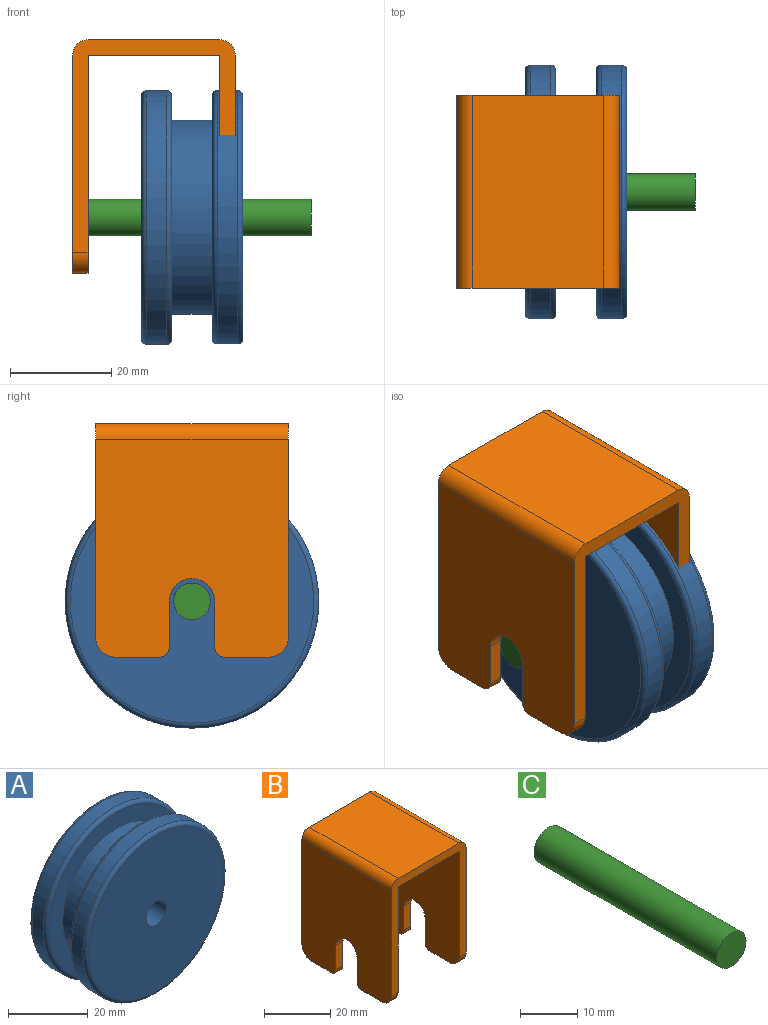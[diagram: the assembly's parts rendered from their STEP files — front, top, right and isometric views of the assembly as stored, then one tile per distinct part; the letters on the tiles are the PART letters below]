
ASSEMBLY  parts=3 mates=2
PART A: 12 faces, bbox 54.1x20x54.1 mm
  f0: cylinder r=25mm len=50mm, axis (0,-1,0), area 628.3mm2, adj f10,f11
  f1: plane 48x48mm, normal (0,1,0), area 660.5mm2, adj f3,f11
  f2: plane 48x48mm, normal (0,-1,0), area 1768.8mm2, adj f7,f10
  f3: cylinder r=19.12mm len=38.25mm, axis (0,-1,0), area 961.3mm2, adj f1,f6
  f4: cylinder r=25mm len=50mm, axis (0,-1,0), area 628.3mm2, adj f8,f9
  f5: plane 48x48mm, normal (0,1,0), area 1768.8mm2, adj f7,f9
  f6: plane 48x48mm, normal (0,-1,0), area 660.5mm2, adj f3,f8
  f7: cylinder r=3.6mm len=20mm, axis (0,1,0), area 452.4mm2, adj f2,f5
  f8: torus R=24mm, axis (0,1,0), area 243.2mm2, adj f4,f6
  f9: torus R=24mm, axis (0,1,0), area 243.2mm2, adj f4,f5
  f10: torus R=24mm, axis (0,-1,0), area 243.2mm2, adj f0,f2
  f11: torus R=24mm, axis (0,-1,0), area 243.2mm2, adj f0,f1
PART B: 28 faces, bbox 32x38x46 mm
  f0: plane 8.5x3mm, normal (0,0,-1), area 25.5mm2, adj f2,f3,f22,f25
  f1: plane 8.5x3mm, normal (0,0,-1), area 25.5mm2, adj f4,f9,f20,f26
  f2: plane 43x38mm, normal (-1,0,0), area 1494.6mm2, adj f0,f6,f10,f11,f12,f17,f18,f19
  f3: plane 43x38mm, normal (1,0,0), area 1494.6mm2, adj f0,f6,f7,f10,f11,f17,f18,f19
  f4: plane 43x38mm, normal (-1,0,0), area 1494.6mm2, adj f1,f7,f8,f10,f11,f14,f15,f16
  f5: plane 38x26mm, normal (0,0,1), area 988mm2, adj f10,f11,f12,f13
  f6: plane 8.5x3mm, normal (0,0,-1), area 25.5mm2, adj f2,f3,f23,f27
  f7: plane 38x26mm, normal (0,0,-1), area 988mm2, adj f3,f4,f10,f11
  f8: plane 8.5x3mm, normal (0,0,-1), area 25.5mm2, adj f4,f9,f21,f24
  f9: plane 43x38mm, normal (1,0,0), area 1494.6mm2, adj f1,f8,f10,f11,f13,f14,f15,f16
  f10: plane 42x32mm, normal (0,1,0), area 326.1mm2, adj f2,f3,f4,f5,f7,f9,f12,f13
  f11: plane 42x32mm, normal (0,-1,0), area 326.1mm2, adj f2,f3,f4,f5,f7,f9,f12,f13
  f12: cylinder r=3mm len=38mm, axis (0,-1,0), area 179.1mm2, adj f2,f5,f10,f11
  f13: cylinder r=3mm len=38mm, axis (0,-1,0), area 179.1mm2, adj f5,f9,f10,f11
  f14: cylinder r=4.5mm len=9mm, axis (1,0,0), area 42.4mm2, adj f4,f9,f15,f16
  f15: plane 9x3mm, normal (0,1,0), area 27mm2, adj f4,f9,f14,f21
  f16: plane 9x3mm, normal (0,-1,0), area 27mm2, adj f4,f9,f14,f20
  f17: plane 9x3mm, normal (0,-1,0), area 27mm2, adj f2,f3,f19,f23
  f18: plane 9x3mm, normal (0,1,0), area 27mm2, adj f2,f3,f19,f22
  f19: cylinder r=4.5mm len=9mm, axis (1,0,0), area 42.4mm2, adj f2,f3,f17,f18
  f20: cylinder r=2mm len=3mm, axis (-1,0,0), area 9.4mm2, adj f1,f4,f9,f16
  f21: cylinder r=2mm len=3mm, axis (1,0,0), area 9.4mm2, adj f4,f8,f9,f15
  f22: cylinder r=2mm len=3mm, axis (-1,0,0), area 9.4mm2, adj f0,f2,f3,f18
  f23: cylinder r=2mm len=3mm, axis (1,0,0), area 9.4mm2, adj f2,f3,f6,f17
  f24: cylinder r=4mm len=4mm, axis (1,0,0), area 18.8mm2, adj f4,f8,f9,f11
  f25: cylinder r=4mm len=4mm, axis (1,0,0), area 18.8mm2, adj f0,f2,f3,f11
  f26: cylinder r=4mm len=4mm, axis (-1,0,0), area 18.8mm2, adj f1,f4,f9,f10
  f27: cylinder r=4mm len=4mm, axis (-1,0,0), area 18.8mm2, adj f2,f3,f6,f10
PART C: 3 faces, bbox 7.2x45x7.2 mm
  f0: cylinder r=3.6mm len=45mm, axis (0,-1,0), area 1017.9mm2, adj f1,f2
  f1: plane 7.2x7.2mm, normal (0,1,0), area 40.7mm2, adj f0
  f2: plane 7.2x7.2mm, normal (0,-1,0), area 40.7mm2, adj f0
PLACE A rot(axis=(0.06,0.06,-1),90.2deg) t=(10.5,0,0)mm
PLACE B t=(-3,-19,-11)mm
PLACE C rot(axis=(-0.58,0.58,0.58),120deg) t=(44,0,0)mm
MATE fastened C.f0 <-> B.f14  axis (1,0,0) through (44,0,0)mm
MATE revolute A.f7 <-> C.f0  axis (1,0,0) through (20.5,0,0)mm
